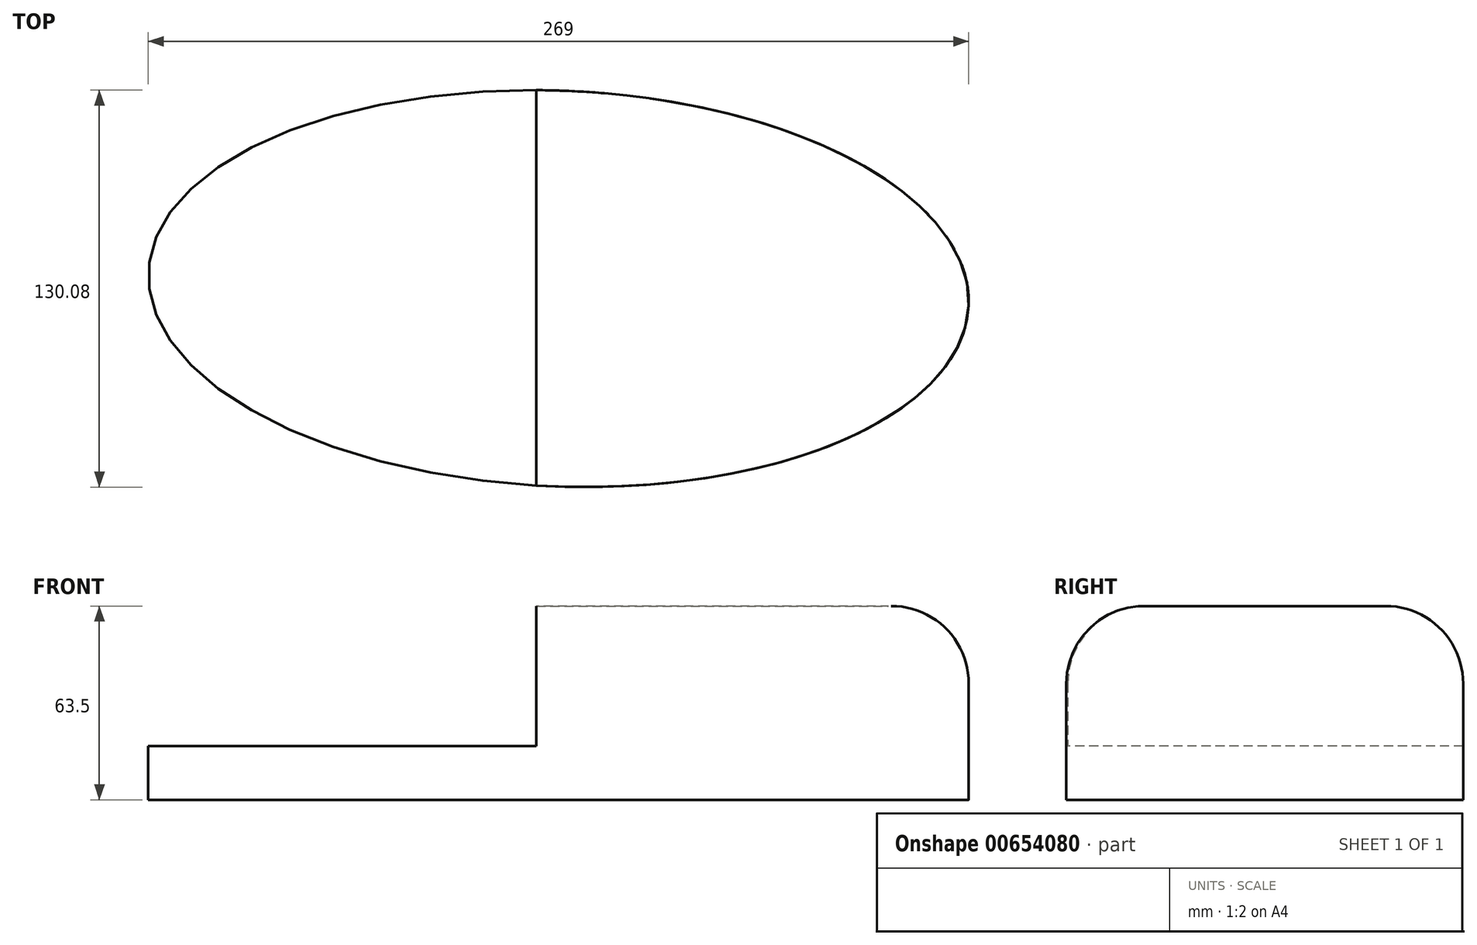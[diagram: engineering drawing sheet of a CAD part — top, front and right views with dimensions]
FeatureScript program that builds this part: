
annotation { "Feature Type Name" : "Feature", "Feature Type Description" : "" }
export const myFeature = defineFeature(function(context is Context, id is Id, definition is map)
    precondition{}
    {
        {
            var Q0;
            Q0=qCreatedBy(makeId("Top.planeOp"),FACE);
            var sketch = newSketch(context, id + "F0", { "sketchPlane" : qUnion([Q0])});
            skEllipse(sketch, "E0", {"center": v(0, 0) * mm, "majorRadius": 134.59 * mm, "minorRadius": 64.86 * mm, "majorAxis": v(1, -0.04)});
            skSolve(sketch);
        }
        {
            var Q0;
            Q0 = qSketchRegion(id + "F0", true);
            extrude(context, id + "F1", {"entities" : qUnion([Q0]), "depth" : 63.5 * mm, "offsetDistance" : 25.4 * mm});
        }
        {
            var Q0;
            Q0=makeQuery(id+"F1.opExtrude","CAP_EDGE",EDGE,{"disambiguationData":[OSD([sQuery(id+"F0.wireOp",EDGE,"E0")])],"isStart":false});
            fillet(context, id + "F2", {"entities" : qUnion([Q0]), "radius" : 25.4 * mm, "tangentPropagation" : true, "allowEdgeOverflow" : false});
        }
        {
            var Q0;
            Q0=qCreatedBy(makeId("Front.planeOp"),FACE);
            var sketch = newSketch(context, id + "F3", { "sketchPlane" : qUnion([Q0])});
            skLineSegment(sketch, "E1.bottom", {"start": v(-7.25, 69.73) * mm, "end": v(-234.55, 69.73) * mm});
            skLineSegment(sketch, "E1.top", {"start": v(-7.25, 17.6) * mm, "end": v(-234.55, 17.6) * mm});
            skLineSegment(sketch, "E1.left", {"start": v(-7.25, 69.73) * mm, "end": v(-7.25, 17.6) * mm});
            skLineSegment(sketch, "E1.right", {"start": v(-234.55, 69.73) * mm, "end": v(-234.55, 17.6) * mm});
            skSolve(sketch);
        }
        {
            var Q0;
            Q0=makeQuery(id+"F3.imprint","IMPRINT",FACE,{"disambiguationData":[TD([[makeQuery(id+"F3.imprint","IMPRINT",EDGE,{"derivedFrom":sQuery(id+"F3.wireOp",EDGE,"E1.bottom")}),1.0]])]});
            extrude(context, id + "F4", {"entities" : qUnion([Q0]), "operationType" : NewBodyOperationType.REMOVE, "endBound" : BoundingType.SYMMETRIC, "oppositeDirection" : true, "depth" : 177.8 * mm, "offsetDistance" : 25.4 * mm});
        }
    });
